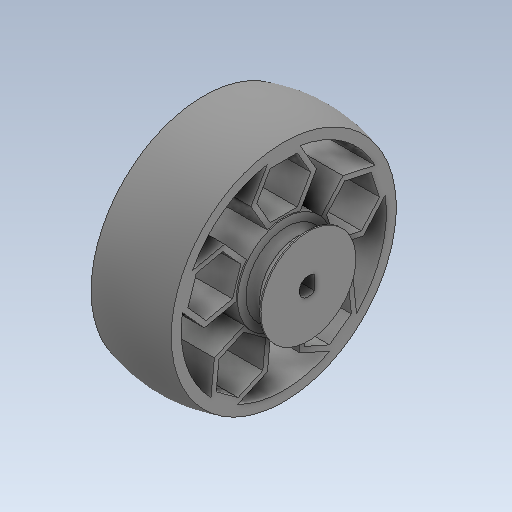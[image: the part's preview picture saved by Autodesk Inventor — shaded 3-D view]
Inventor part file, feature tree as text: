
AUTODESK INVENTOR PART (.ipt)
format: ipt  version: 2020 (Build 240168000, 168)  size: 398,336 bytes
history: native  units: in
note: dims shown in document units (in); Inventor stores cm internally (conversion verified against a paired STEP export)
features: sketch x4, extrude x2, revolve x2, projected_geometry x1
ambient origin geometry x8: Origin, YZ Plane, XZ Plane, XY Plane, X Axis, Y Axis, Z Axis, Center Point
bodies: Solid1 (feature_tree)
feature tree (9):
  extrude  "Extrusion1"  Depth=0.0394in
  sketch  "Sketch3"  dims[d6=0.6063in d7=0.1575in]
  revolve  "Revolution1"  [1 undecoded]
  extrude  "Extrusion2"  Depth=0.1575in
  revolve  "Revolution2"  [1 undecoded]
  sketch  "Sketch1"  dims[d0=0.1181in d1=0.0394in]
  sketch  "Sketch2"  dims[d3=1.437in d4=0.1181in]
  projected_geometry  "Projected Loop1"
  sketch  "Sketch4"  dims[d8=0.0in d9=1.437in d10=0.063in d11=0.0315in d16=0.5118in d17=0.0in d19=360.0deg d20=0.0787in d24=0.0394in d25=90.0deg d26=45.0deg d28=0.0079in d29=1.9685in d31=360.0deg]
note: 2 required parameter values undecoded (feature->parameter linkage not recoverable at this tier; creation-order binding heuristic only, values carry confidence <= 0.55)
